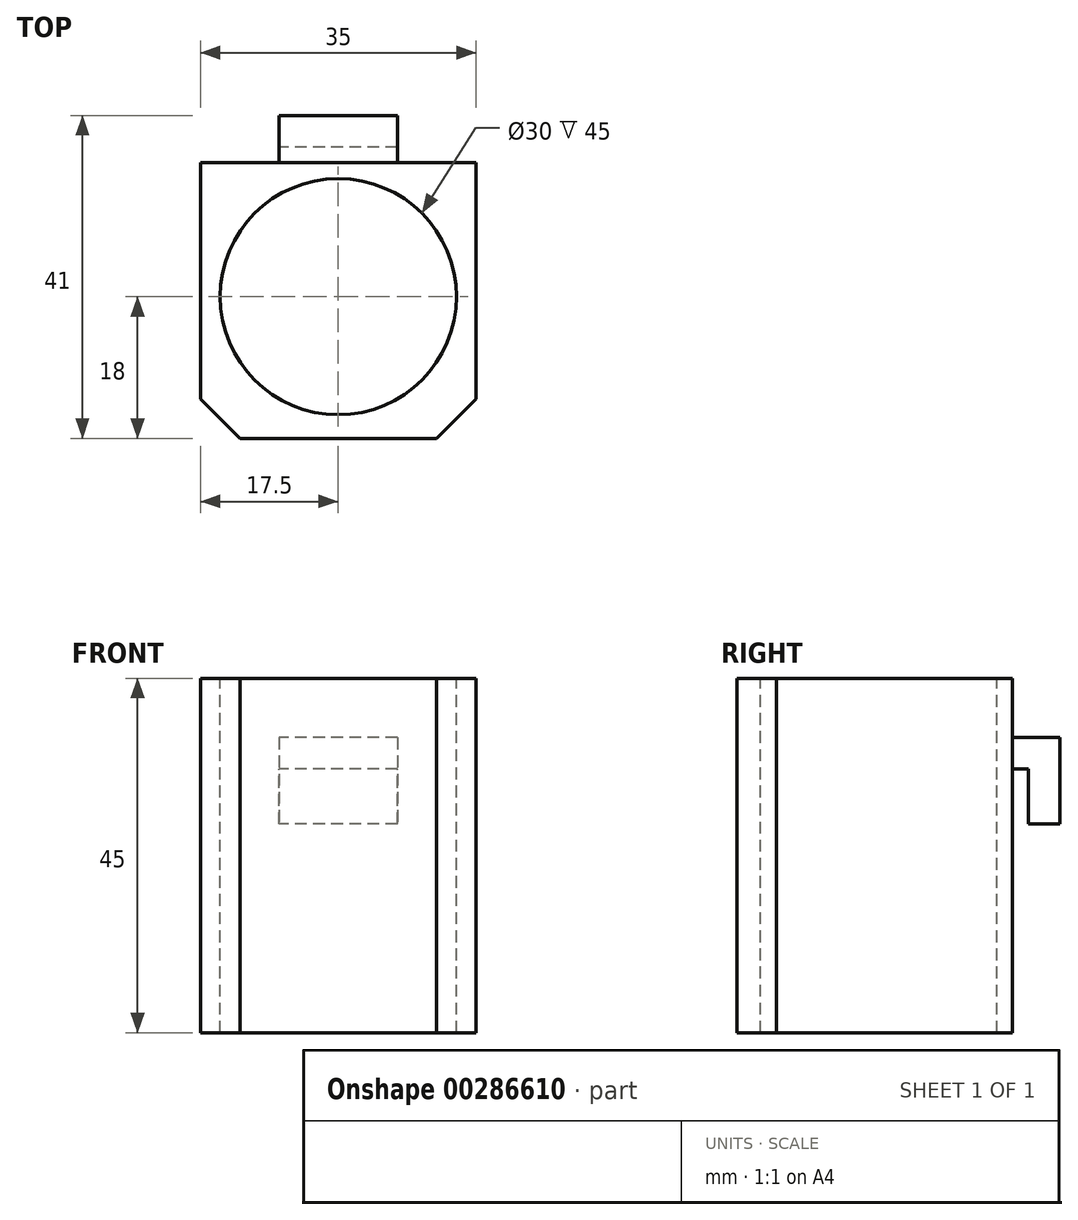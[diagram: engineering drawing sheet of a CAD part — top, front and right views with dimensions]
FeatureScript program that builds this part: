
annotation { "Feature Type Name" : "Feature", "Feature Type Description" : "" }
export const myFeature = defineFeature(function(context is Context, id is Id, definition is map)
    precondition{}
    {
        {
            var Q0;
            Q0=qCreatedBy(makeId("Front.planeOp"),FACE);
            var sketch = newSketch(context, id + "F0", { "sketchPlane" : qUnion([Q0])});
            skLineSegment(sketch, "E0.bottom", {"start": v(-17.5, 22.5) * mm, "end": v(17.5, 22.5) * mm});
            skLineSegment(sketch, "E0.top", {"start": v(-17.5, -22.5) * mm, "end": v(17.5, -22.5) * mm});
            skLineSegment(sketch, "E0.left", {"start": v(-17.5, 22.5) * mm, "end": v(-17.5, -22.5) * mm});
            skLineSegment(sketch, "E0.right", {"start": v(17.5, 22.5) * mm, "end": v(17.5, -22.5) * mm});
            skPoint(sketch, "E0.middle", {"position": v(0, 0) * mm});
            skSolve(sketch);
        }
        {
            var Q0;
            Q0=makeQuery(id+"F0.imprint","IMPRINT",FACE,{"disambiguationData":[TD([[makeQuery(id+"F0.imprint","IMPRINT",EDGE,{"derivedFrom":sQuery(id+"F0.wireOp",EDGE,"E0.bottom")}),-1.0]])]});
            extrude(context, id + "F1", {"entities" : qUnion([Q0]), "depth" : 35 * mm});
        }
        {
            var Q0;
            Q0=makeQuery(id+"F1.opExtrude","CAP_FACE",FACE,{"disambiguationData":[OSD([sQuery(id+"F0.wireOp",EDGE,"E0.bottom"),sQuery(id+"F0.wireOp",EDGE,"E0.top"),sQuery(id+"F0.wireOp",EDGE,"E0.left"),sQuery(id+"F0.wireOp",EDGE,"E0.right")])],"isStart":true});
            var sketch = newSketch(context, id + "F2", { "sketchPlane" : qUnion([Q0])});
            skLineSegment(sketch, "E1.bottom", {"start": v(-7.5, 15) * mm, "end": v(7.5, 15) * mm});
            skLineSegment(sketch, "E1.top", {"start": v(-7.5, 11) * mm, "end": v(7.5, 11) * mm});
            skLineSegment(sketch, "E1.left", {"start": v(-7.5, 15) * mm, "end": v(-7.5, 11) * mm});
            skLineSegment(sketch, "E1.right", {"start": v(7.5, 15) * mm, "end": v(7.5, 11) * mm});
            skPoint(sketch, "E1.middle", {"position": v(0, 13) * mm});
            skSolve(sketch);
        }
        {
            var Q0;
            Q0=makeQuery(id+"F2.imprint","IMPRINT",FACE,{"disambiguationData":[TD([[makeQuery(id+"F2.imprint","IMPRINT",EDGE,{"derivedFrom":sQuery(id+"F2.wireOp",EDGE,"E1.bottom")}),-1.0]])]});
            extrude(context, id + "F3", {"entities" : qUnion([Q0]), "operationType" : NewBodyOperationType.ADD, "depth" : 6 * mm});
        }
        {
            var Q0;
            Q0=makeQuery(id+"F3.opExtrude","SWEPT_FACE",FACE,{"disambiguationData":[OSD([sQuery(id+"F2.wireOp",EDGE,"E1.top")])]});
            var sketch = newSketch(context, id + "F4", { "sketchPlane" : qUnion([Q0])});
            skLineSegment(sketch, "E2.bottom", {"start": v(7.5, -6) * mm, "end": v(-7.5, -6) * mm});
            skLineSegment(sketch, "E2.top", {"start": v(7.5, -2) * mm, "end": v(-7.5, -2) * mm});
            skLineSegment(sketch, "E2.left", {"start": v(7.5, -6) * mm, "end": v(7.5, -2) * mm});
            skLineSegment(sketch, "E2.right", {"start": v(-7.5, -6) * mm, "end": v(-7.5, -2) * mm});
            skSolve(sketch);
        }
        {
            var Q0;
            Q0=makeQuery(id+"F4.imprint","IMPRINT",FACE,{"disambiguationData":[TD([[makeQuery(id+"F4.imprint","IMPRINT",EDGE,{"derivedFrom":sQuery(id+"F4.wireOp",EDGE,"E2.bottom")}),-1.0]])]});
            extrude(context, id + "F5", {"entities" : qUnion([Q0]), "operationType" : NewBodyOperationType.ADD, "depth" : 7 * mm});
        }
        {
            var Q0;
            Q0=makeQuery(id+"F1.opExtrude","CAP_EDGE",EDGE,{"disambiguationData":[OSD([sQuery(id+"F0.wireOp",EDGE,"E0.left")])],"isStart":false});
            var Q1;
            Q1=makeQuery(id+"F1.opExtrude","CAP_EDGE",EDGE,{"disambiguationData":[OSD([sQuery(id+"F0.wireOp",EDGE,"E0.right")])],"isStart":false});
            chamfer(context, id + "F6", {"entities" : qUnion([Q0, Q1]), "width" : 5 * mm, "tangentPropagation" : true});
        }
        {
            var Q0;
            Q0=makeQuery(id+"F1.opExtrude","SWEPT_FACE",FACE,{"disambiguationData":[OSD([sQuery(id+"F0.wireOp",EDGE,"E0.bottom")])]});
            var sketch = newSketch(context, id + "F7", { "sketchPlane" : qUnion([Q0])});
            skCircle(sketch, "E3", {"center": v(0, -17) * mm, "radius": 15 * mm});
            skPoint(sketch, "E3.centerSnap0", {"position": v(17.5, -17) * mm});
            skSolve(sketch);
        }
        {
            var Q0;
            Q0=makeQuery(id+"F7.imprint","IMPRINT",FACE,{"disambiguationData":[TD([[makeQuery(id+"F7.imprint","IMPRINT",EDGE,{"derivedFrom":sQuery(id+"F7.wireOp",EDGE,"E3")}),1.0]])]});
            extrude(context, id + "F8", {"entities" : qUnion([Q0]), "operationType" : NewBodyOperationType.REMOVE, "endBound" : BoundingType.THROUGH_ALL, "oppositeDirection" : true, "depth" : 25 * mm});
        }
    });
